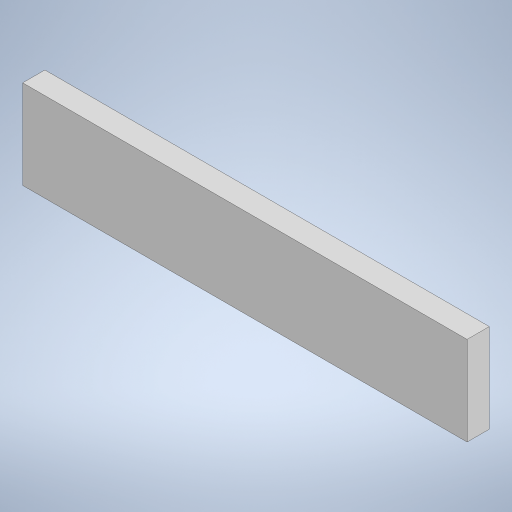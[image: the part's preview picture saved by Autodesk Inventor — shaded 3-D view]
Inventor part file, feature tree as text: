
AUTODESK INVENTOR PART (.ipt)
format: ipt  version: 2024.1 (Build 281209000, 209)  size: 204,800 bytes
history: native  units: mm
features: other x1, extrude x1, sketch x1
ambient origin geometry x8: Origin, YZ Plane, XZ Plane, XY Plane, X Axis, Y Axis, Z Axis, Center Point
bodies: Body1 (feature_tree)
feature tree (3):
  other  "ソリッド1"
  extrude  "押し出し1"  Depth=50.0mm
  sketch  "スケッチ1"
